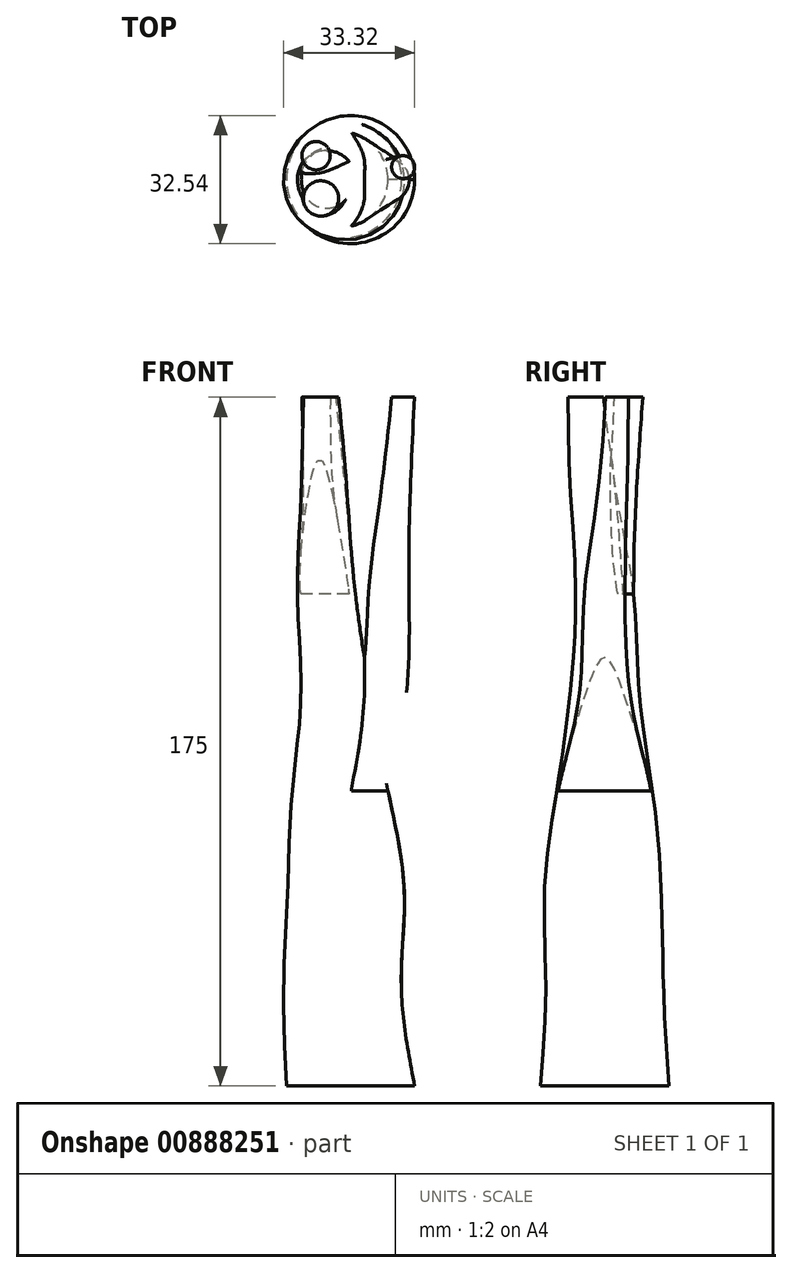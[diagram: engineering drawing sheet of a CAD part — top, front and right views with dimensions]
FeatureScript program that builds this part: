
annotation { "Feature Type Name" : "Feature", "Feature Type Description" : "" }
export const myFeature = defineFeature(function(context is Context, id is Id, definition is map)
    precondition{}
    {
        {
            var Q0;
            Q0=qCreatedBy(makeId("Top.planeOp"),FACE);
            cPlane(context, id + "F0", {"entities" : qUnion([Q0]), "cplaneType" : CPlaneType.OFFSET, "offset" : 25 * mm, "width" : 150 * mm, "height" : 150 * mm});
        }
        {
            var Q0;
            Q0=qCreatedBy(id+"F0.planeOp",FACE);
            cPlane(context, id + "F1", {"entities" : qUnion([Q0]), "cplaneType" : CPlaneType.OFFSET, "offset" : 25 * mm, "width" : 150 * mm, "height" : 150 * mm});
        }
        {
            var Q0;
            Q0=qCreatedBy(id+"F1.planeOp",FACE);
            cPlane(context, id + "F2", {"entities" : qUnion([Q0]), "cplaneType" : CPlaneType.OFFSET, "offset" : 25 * mm, "width" : 150 * mm, "height" : 150 * mm});
        }
        {
            var Q0;
            Q0=qCreatedBy(id+"F2.planeOp",FACE);
            cPlane(context, id + "F3", {"entities" : qUnion([Q0]), "cplaneType" : CPlaneType.OFFSET, "offset" : 25 * mm, "width" : 150 * mm, "height" : 150 * mm});
        }
        {
            var Q0;
            Q0=qCreatedBy(id+"F3.planeOp",FACE);
            cPlane(context, id + "F4", {"entities" : qUnion([Q0]), "cplaneType" : CPlaneType.OFFSET, "offset" : 25 * mm, "width" : 150 * mm, "height" : 150 * mm});
        }
        {
            var Q0;
            Q0=qCreatedBy(makeId("Top.planeOp"),FACE);
            var sketch = newSketch(context, id + "F5", { "sketchPlane" : qUnion([Q0])});
            skCircle(sketch, "E0", {"center": v(0, 0) * mm, "radius": 16.27 * mm});
            skSolve(sketch);
        }
        {
            var Q0;
            Q0=qCreatedBy(id+"F0.planeOp",FACE);
            var sketch = newSketch(context, id + "F6", { "sketchPlane" : qUnion([Q0])});
            skCircle(sketch, "E1", {"center": v(-2.08, 0) * mm, "radius": 14.96 * mm});
            skSolve(sketch);
        }
        {
            var Q0;
            Q0=qCreatedBy(id+"F1.planeOp",FACE);
            var sketch = newSketch(context, id + "F7", { "sketchPlane" : qUnion([Q0])});
            skCircle(sketch, "E2", {"center": v(-1.2, -0.45) * mm, "radius": 14.8 * mm});
            skSolve(sketch);
        }
        {
            var Q0;
            Q0=qCreatedBy(id+"F2.planeOp",FACE);
            var sketch = newSketch(context, id + "F8", { "sketchPlane" : qUnion([Q0])});
            skCircle(sketch, "E3", {"center": v(-2.66, 0) * mm, "radius": 12.16 * mm});
            skSolve(sketch);
        }
        {
            var Q0;
            Q0=qCreatedBy(id+"F3.planeOp",FACE);
            var sketch = newSketch(context, id + "F9", { "sketchPlane" : qUnion([Q0])});
            skCircle(sketch, "E4", {"center": v(-3.83, 0) * mm, "radius": 8.73 * mm});
            skSolve(sketch);
        }
        {
            var Q0;
            Q0=qCreatedBy(id+"F3.planeOp",FACE);
            var sketch = newSketch(context, id + "F10", { "sketchPlane" : qUnion([Q0])});
            skCircle(sketch, "E5", {"center": v(7.8, 0) * mm, "radius": 6.4 * mm});
            skSolve(sketch);
        }
        {
            var Q0;
            Q0=qCreatedBy(id+"F4.planeOp",FACE);
            var sketch = newSketch(context, id + "F11", { "sketchPlane" : qUnion([Q0])});
            skCircle(sketch, "E6", {"center": v(9.66, 0) * mm, "radius": 5.17 * mm});
            skSolve(sketch);
        }
        {
            var Q0;
            Q0=qCreatedBy(id+"F4.planeOp",FACE);
            var sketch = newSketch(context, id + "F12", { "sketchPlane" : qUnion([Q0])});
            skCircle(sketch, "E7", {"center": v(-6.15, 0) * mm, "radius": 7.37 * mm});
            skSolve(sketch);
        }
        {
            var Q0;
            Q0=qCreatedBy(id+"F4.planeOp",FACE);
            cPlane(context, id + "F13", {"entities" : qUnion([Q0]), "cplaneType" : CPlaneType.OFFSET, "offset" : 25 * mm, "width" : 150 * mm, "height" : 150 * mm});
        }
        {
            var Q0;
            Q0=qCreatedBy(id+"F13.planeOp",FACE);
            cPlane(context, id + "F14", {"entities" : qUnion([Q0]), "cplaneType" : CPlaneType.OFFSET, "offset" : 25 * mm, "width" : 150 * mm, "height" : 150 * mm});
        }
        {
            var Q0;
            Q0=qCreatedBy(id+"F13.planeOp",FACE);
            var sketch = newSketch(context, id + "F15", { "sketchPlane" : qUnion([Q0])});
            skCircle(sketch, "E8", {"center": v(-8.1, 4.17) * mm, "radius": 3.82 * mm});
            skSolve(sketch);
        }
        {
            var Q0;
            Q0=qCreatedBy(id+"F13.planeOp",FACE);
            var sketch = newSketch(context, id + "F16", { "sketchPlane" : qUnion([Q0])});
            skCircle(sketch, "E9", {"center": v(-6.73, -2.76) * mm, "radius": 5.9 * mm});
            skSolve(sketch);
        }
        {
            var Q0;
            Q0=qCreatedBy(id+"F13.planeOp",FACE);
            var sketch = newSketch(context, id + "F17", { "sketchPlane" : qUnion([Q0])});
            skCircle(sketch, "E10", {"center": v(11.36, 1.9) * mm, "radius": 3.76 * mm});
            skSolve(sketch);
        }
        {
            var Q0;
            Q0=qCreatedBy(id+"F14.planeOp",FACE);
            var sketch = newSketch(context, id + "F18", { "sketchPlane" : qUnion([Q0])});
            skCircle(sketch, "E11", {"center": v(-8.78, 6.07) * mm, "radius": 3.6 * mm});
            skSolve(sketch);
        }
        {
            var Q0;
            Q0=qCreatedBy(id+"F14.planeOp",FACE);
            var sketch = newSketch(context, id + "F19", { "sketchPlane" : qUnion([Q0])});
            skCircle(sketch, "E12", {"center": v(-7.54, -4.79) * mm, "radius": 4.49 * mm});
            skSolve(sketch);
        }
        {
            var Q0;
            Q0=qCreatedBy(id+"F14.planeOp",FACE);
            var sketch = newSketch(context, id + "F20", { "sketchPlane" : qUnion([Q0])});
            skCircle(sketch, "E13", {"center": v(13.34, 3.18) * mm, "radius": 2.92 * mm});
            skSolve(sketch);
        }
        {
            var Q0;
            Q0=makeQuery(id+"F5.imprint","IMPRINT",FACE,{"disambiguationData":[TD([[makeQuery(id+"F5.imprint","IMPRINT",EDGE,{"derivedFrom":sQuery(id+"F5.wireOp",EDGE,"E0")}),1.0]])]});
            var Q1;
            Q1=makeQuery(id+"F6.imprint","IMPRINT",FACE,{"disambiguationData":[TD([[makeQuery(id+"F6.imprint","IMPRINT",EDGE,{"derivedFrom":sQuery(id+"F6.wireOp",EDGE,"E1")}),1.0]])]});
            var Q2;
            Q2=makeQuery(id+"F7.imprint","IMPRINT",FACE,{"disambiguationData":[TD([[makeQuery(id+"F7.imprint","IMPRINT",EDGE,{"derivedFrom":sQuery(id+"F7.wireOp",EDGE,"E2")}),1.0]])]});
            var Q3;
            Q3=makeQuery(id+"F8.imprint","IMPRINT",FACE,{"disambiguationData":[TD([[makeQuery(id+"F8.imprint","IMPRINT",EDGE,{"derivedFrom":sQuery(id+"F8.wireOp",EDGE,"E3")}),1.0]])]});
            var Q4;
            Q4=makeQuery(id+"F9.imprint","IMPRINT",FACE,{"disambiguationData":[TD([[makeQuery(id+"F9.imprint","IMPRINT",EDGE,{"derivedFrom":sQuery(id+"F9.wireOp",EDGE,"E4")}),1.0]])]});
            var Q5;
            Q5=makeQuery(id+"F12.imprint","IMPRINT",FACE,{"disambiguationData":[TD([[makeQuery(id+"F12.imprint","IMPRINT",EDGE,{"derivedFrom":sQuery(id+"F12.wireOp",EDGE,"E7")}),1.0]])]});
            var Q6;
            Q6=makeQuery(id+"F16.imprint","IMPRINT",FACE,{"disambiguationData":[TD([[makeQuery(id+"F16.imprint","IMPRINT",EDGE,{"derivedFrom":sQuery(id+"F16.wireOp",EDGE,"E9")}),1.0]])]});
            var Q7;
            Q7=makeQuery(id+"F19.imprint","IMPRINT",FACE,{"disambiguationData":[TD([[makeQuery(id+"F19.imprint","IMPRINT",EDGE,{"derivedFrom":sQuery(id+"F19.wireOp",EDGE,"E12")}),1.0]])]});
            loft(context, id + "F21", {"sheetProfilesArray" : [{ "sheetProfileEntities" : qUnion([Q0]) }, { "sheetProfileEntities" : qUnion([Q1]) }, { "sheetProfileEntities" : qUnion([Q2]) }, { "sheetProfileEntities" : qUnion([Q3]) }, { "sheetProfileEntities" : qUnion([Q4]) }, { "sheetProfileEntities" : qUnion([Q5]) }, { "sheetProfileEntities" : qUnion([Q6]) }, { "sheetProfileEntities" : qUnion([Q7]) }]});
        }
        {
            var Q1;
            Q1 = qSketchRegion(id + "F8", true);
            var Q2;
            Q2 = qSketchRegion(id + "F10", true);
            var Q3;
            Q3 = qSketchRegion(id + "F11", true);
            var Q4;
            Q4 = qSketchRegion(id + "F17", true);
            var Q5;
            Q5 = qSketchRegion(id + "F20", true);
            loft(context, id + "F22", {"operationType" : NewBodyOperationType.ADD, "sheetProfilesArray" : [{ "sheetProfileEntities" : qUnion([Q1]) }, { "sheetProfileEntities" : qUnion([Q2]) }, { "sheetProfileEntities" : qUnion([Q3]) }, { "sheetProfileEntities" : qUnion([Q4]) }, { "sheetProfileEntities" : qUnion([Q5]) }]});
        }
        {
            var Q1;
            Q1 = qSketchRegion(id + "F12", true);
            var Q2;
            Q2=makeQuery(id+"F15.imprint","IMPRINT",FACE,{"disambiguationData":[TD([[makeQuery(id+"F15.imprint","IMPRINT",EDGE,{"derivedFrom":sQuery(id+"F15.wireOp",EDGE,"E8")}),1.0]])]});
            var Q3;
            Q3=makeQuery(id+"F18.imprint","IMPRINT",FACE,{"disambiguationData":[TD([[makeQuery(id+"F18.imprint","IMPRINT",EDGE,{"derivedFrom":sQuery(id+"F18.wireOp",EDGE,"E11")}),1.0]])]});
            loft(context, id + "F23", {"operationType" : NewBodyOperationType.ADD, "sheetProfilesArray" : [{ "sheetProfileEntities" : qUnion([Q1]) }, { "sheetProfileEntities" : qUnion([Q2]) }, { "sheetProfileEntities" : qUnion([Q3]) }]});
        }
    });
